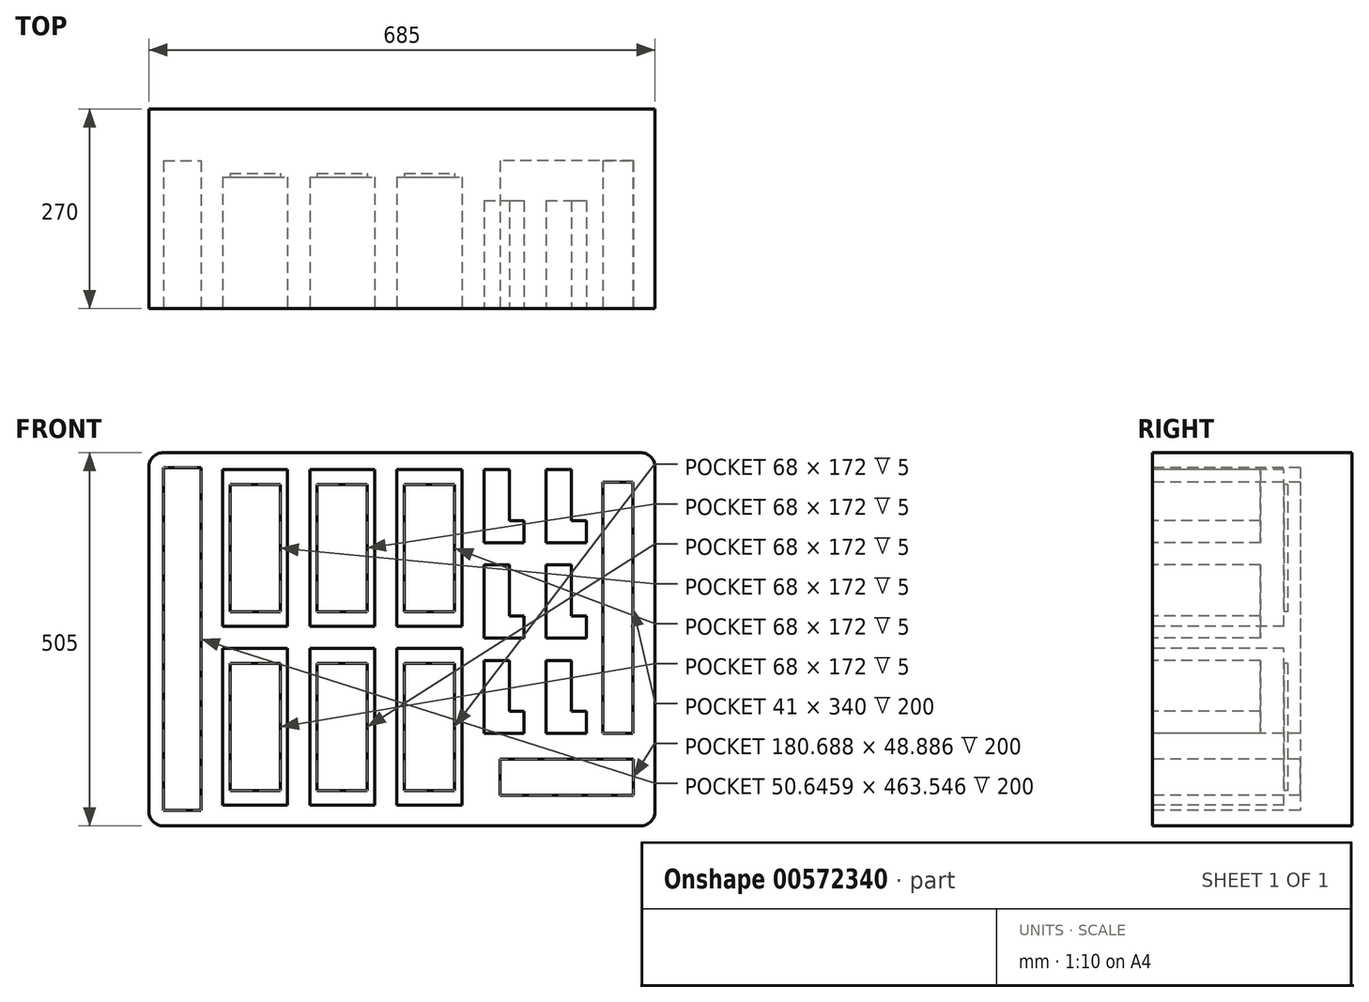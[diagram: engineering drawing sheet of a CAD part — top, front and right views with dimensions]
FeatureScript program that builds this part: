
annotation { "Feature Type Name" : "Feature", "Feature Type Description" : "" }
export const myFeature = defineFeature(function(context is Context, id is Id, definition is map)
    precondition{}
    {
        {
            var Q0;
            Q0=qCreatedBy(makeId("Front.planeOp"),FACE);
            var sketch = newSketch(context, id + "F0", { "sketchPlane" : qUnion([Q0])});
            skLineSegment(sketch, "E0.bottom", {"start": v(-665, 505) * mm, "end": v(-20, 505) * mm});
            skLineSegment(sketch, "E0.top", {"start": v(-665, 0) * mm, "end": v(-20, 0) * mm});
            skLineSegment(sketch, "E0.left", {"start": v(-685, 485) * mm, "end": v(-685, 20) * mm});
            skLineSegment(sketch, "E0.right", {"start": v(0, 485) * mm, "end": v(0, 20) * mm});
            skPoint(sketch, "E1.visualSharp", {"position": v(-685, 505) * mm});
            skArc(sketch, "E1.filletArc", {"start": v(-665, 505) * mm, "mid": v(-679.14, 499.14) * mm, "end": v(-685, 485) * mm});
            skPoint(sketch, "E2.visualSharp", {"position": v(-685, 0) * mm});
            skArc(sketch, "E2.filletArc", {"start": v(-685, 20) * mm, "mid": v(-679.14, 5.86) * mm, "end": v(-665, 0) * mm});
            skPoint(sketch, "E3.visualSharp", {"position": v(0, 0) * mm});
            skArc(sketch, "E3.filletArc", {"start": v(-20, 0) * mm, "mid": v(-5.86, 5.86) * mm, "end": v(0, 20) * mm});
            skPoint(sketch, "E4.visualSharp", {"position": v(0, 505) * mm});
            skArc(sketch, "E4.filletArc", {"start": v(0, 485) * mm, "mid": v(-5.86, 499.14) * mm, "end": v(-20, 505) * mm});
            skSolve(sketch);
        }
        {
            var Q0;
            Q0=makeQuery(id+"F0.imprint","IMPRINT",FACE,{"disambiguationData":[TD([[makeQuery(id+"F0.imprint","IMPRINT",EDGE,{"derivedFrom":sQuery(id+"F0.wireOp",EDGE,"E0.bottom")}),-1.0]])]});
            extrude(context, id + "F1", {"entities" : qUnion([Q0]), "oppositeDirection" : true, "depth" : 270 * mm, "offsetDistance" : 25 * mm});
        }
        {
            var Q0;
            Q0=makeQuery(id+"F1.opExtrude","CAP_FACE",FACE,{"disambiguationData":[OSD([sQuery(id+"F0.wireOp",EDGE,"E0.bottom"),sQuery(id+"F0.wireOp",EDGE,"E0.top"),sQuery(id+"F0.wireOp",EDGE,"E0.left"),sQuery(id+"F0.wireOp",EDGE,"E0.right")])],"isStart":true});
            var sketch = newSketch(context, id + "F2", { "sketchPlane" : qUnion([Q0])});
            skLineSegment(sketch, "E5.bottom", {"start": v(-585.25, 28) * mm, "end": v(-497.25, 28) * mm});
            skLineSegment(sketch, "E5.top", {"start": v(-585.25, 240) * mm, "end": v(-497.25, 240) * mm});
            skLineSegment(sketch, "E5.left", {"start": v(-585.25, 28) * mm, "end": v(-585.25, 240) * mm});
            skLineSegment(sketch, "E5.right", {"start": v(-497.25, 28) * mm, "end": v(-497.25, 240) * mm});
            skLineSegment(sketch, "E6.0.1.0", {"start": v(-497.25, 270) * mm, "end": v(-497.25, 482) * mm});
            skLineSegment(sketch, "E6.0.1.1", {"start": v(-585.25, 270) * mm, "end": v(-585.25, 482) * mm});
            skLineSegment(sketch, "E6.0.1.2", {"start": v(-585.25, 482) * mm, "end": v(-497.25, 482) * mm});
            skLineSegment(sketch, "E6.0.1.3", {"start": v(-585.25, 270) * mm, "end": v(-497.25, 270) * mm});
            skLineSegment(sketch, "E6.1.0.0", {"start": v(-379.25, 28) * mm, "end": v(-379.25, 240) * mm});
            skLineSegment(sketch, "E6.1.0.1", {"start": v(-467.25, 28) * mm, "end": v(-467.25, 240) * mm});
            skLineSegment(sketch, "E6.1.0.2", {"start": v(-467.25, 240) * mm, "end": v(-379.25, 240) * mm});
            skLineSegment(sketch, "E6.1.0.3", {"start": v(-467.25, 28) * mm, "end": v(-379.25, 28) * mm});
            skLineSegment(sketch, "E6.1.1.0", {"start": v(-379.25, 270) * mm, "end": v(-379.25, 482) * mm});
            skLineSegment(sketch, "E6.1.1.1", {"start": v(-467.25, 270) * mm, "end": v(-467.25, 482) * mm});
            skLineSegment(sketch, "E6.1.1.2", {"start": v(-467.25, 482) * mm, "end": v(-379.25, 482) * mm});
            skLineSegment(sketch, "E6.1.1.3", {"start": v(-467.25, 270) * mm, "end": v(-379.25, 270) * mm});
            skLineSegment(sketch, "E6.2.0.0", {"start": v(-261.25, 28) * mm, "end": v(-261.25, 240) * mm});
            skLineSegment(sketch, "E6.2.0.1", {"start": v(-349.25, 28) * mm, "end": v(-349.25, 240) * mm});
            skLineSegment(sketch, "E6.2.0.2", {"start": v(-349.25, 240) * mm, "end": v(-261.25, 240) * mm});
            skLineSegment(sketch, "E6.2.0.3", {"start": v(-349.25, 28) * mm, "end": v(-261.25, 28) * mm});
            skLineSegment(sketch, "E6.2.1.0", {"start": v(-261.25, 270) * mm, "end": v(-261.25, 482) * mm});
            skLineSegment(sketch, "E6.2.1.1", {"start": v(-349.25, 270) * mm, "end": v(-349.25, 482) * mm});
            skLineSegment(sketch, "E6.2.1.2", {"start": v(-349.25, 482) * mm, "end": v(-261.25, 482) * mm});
            skLineSegment(sketch, "E6.2.1.3", {"start": v(-349.25, 270) * mm, "end": v(-261.25, 270) * mm});
            skLineSegment(sketch, "E6.direction1", {"start": v(-585.25, 28) * mm, "end": v(-467.25, 28) * mm, "construction": true});
            skLineSegment(sketch, "E6.direction2", {"start": v(-585.25, 28) * mm, "end": v(-585.25, 270) * mm, "construction": true});
            skSolve(sketch);
        }
        {
            var Q0;
            Q0=qSketchRegion(id+"F2",true);
            extrude(context, id + "F3", {"entities" : qUnion([Q0]), "operationType" : NewBodyOperationType.REMOVE, "oppositeDirection" : true, "depth" : 178 * mm, "offsetDistance" : 25 * mm});
        }
        {
            var Q0;
            Q0=makeQuery(id+"F3.boolean.opBoolean","COPY",FACE,{"derivedFrom":makeQuery(id+"F3.opExtrude","CAP_FACE",FACE,{"disambiguationData":[OSD([sQuery(id+"F2.wireOp",EDGE,"E6.0.1.0"),sQuery(id+"F2.wireOp",EDGE,"E6.0.1.1"),sQuery(id+"F2.wireOp",EDGE,"E6.0.1.2"),sQuery(id+"F2.wireOp",EDGE,"E6.0.1.3")])],"isStart":false})});
            var sketch = newSketch(context, id + "F4", { "sketchPlane" : qUnion([Q0])});
            skLineSegment(sketch, "E7.bottom", {"start": v(-575.25, 220) * mm, "end": v(-507.25, 220) * mm});
            skLineSegment(sketch, "E7.top", {"start": v(-575.25, 48) * mm, "end": v(-507.25, 48) * mm});
            skLineSegment(sketch, "E7.left", {"start": v(-575.25, 220) * mm, "end": v(-575.25, 48) * mm});
            skLineSegment(sketch, "E7.right", {"start": v(-507.25, 220) * mm, "end": v(-507.25, 48) * mm});
            skLineSegment(sketch, "E8.0.1.0", {"start": v(-507.25, 462) * mm, "end": v(-507.25, 290) * mm});
            skLineSegment(sketch, "E8.0.1.1", {"start": v(-575.25, 462) * mm, "end": v(-575.25, 290) * mm});
            skLineSegment(sketch, "E8.0.1.2", {"start": v(-575.25, 290) * mm, "end": v(-507.25, 290) * mm});
            skLineSegment(sketch, "E8.0.1.3", {"start": v(-575.25, 462) * mm, "end": v(-507.25, 462) * mm});
            skLineSegment(sketch, "E8.1.0.0", {"start": v(-389.25, 220) * mm, "end": v(-389.25, 48) * mm});
            skLineSegment(sketch, "E8.1.0.1", {"start": v(-457.25, 220) * mm, "end": v(-457.25, 48) * mm});
            skLineSegment(sketch, "E8.1.0.2", {"start": v(-457.25, 48) * mm, "end": v(-389.25, 48) * mm});
            skLineSegment(sketch, "E8.1.0.3", {"start": v(-457.25, 220) * mm, "end": v(-389.25, 220) * mm});
            skLineSegment(sketch, "E8.1.1.0", {"start": v(-389.25, 462) * mm, "end": v(-389.25, 290) * mm});
            skLineSegment(sketch, "E8.1.1.1", {"start": v(-457.25, 462) * mm, "end": v(-457.25, 290) * mm});
            skLineSegment(sketch, "E8.1.1.2", {"start": v(-457.25, 290) * mm, "end": v(-389.25, 290) * mm});
            skLineSegment(sketch, "E8.1.1.3", {"start": v(-457.25, 462) * mm, "end": v(-389.25, 462) * mm});
            skLineSegment(sketch, "E8.2.0.0", {"start": v(-271.25, 220) * mm, "end": v(-271.25, 48) * mm});
            skLineSegment(sketch, "E8.2.0.1", {"start": v(-339.25, 220) * mm, "end": v(-339.25, 48) * mm});
            skLineSegment(sketch, "E8.2.0.2", {"start": v(-339.25, 48) * mm, "end": v(-271.25, 48) * mm});
            skLineSegment(sketch, "E8.2.0.3", {"start": v(-339.25, 220) * mm, "end": v(-271.25, 220) * mm});
            skLineSegment(sketch, "E8.2.1.0", {"start": v(-271.25, 462) * mm, "end": v(-271.25, 290) * mm});
            skLineSegment(sketch, "E8.2.1.1", {"start": v(-339.25, 462) * mm, "end": v(-339.25, 290) * mm});
            skLineSegment(sketch, "E8.2.1.2", {"start": v(-339.25, 290) * mm, "end": v(-271.25, 290) * mm});
            skLineSegment(sketch, "E8.2.1.3", {"start": v(-339.25, 462) * mm, "end": v(-271.25, 462) * mm});
            skLineSegment(sketch, "E8.direction1", {"start": v(-575.25, 48) * mm, "end": v(-457.25, 48) * mm, "construction": true});
            skLineSegment(sketch, "E8.direction2", {"start": v(-575.25, 48) * mm, "end": v(-575.25, 290) * mm, "construction": true});
            skSolve(sketch);
        }
        {
            var Q0;
            Q0=makeQuery(id+"F4.imprint","IMPRINT",FACE,{"disambiguationData":[TD([[makeQuery(id+"F4.imprint","IMPRINT",EDGE,{"derivedFrom":sQuery(id+"F4.wireOp",EDGE,"E8.0.1.0")}),-1.0]])]});
            var Q1;
            Q1=makeQuery(id+"F4.imprint","IMPRINT",FACE,{"disambiguationData":[TD([[makeQuery(id+"F4.imprint","IMPRINT",EDGE,{"derivedFrom":sQuery(id+"F4.wireOp",EDGE,"E8.1.1.0")}),-1.0]])]});
            var Q2;
            Q2=makeQuery(id+"F4.imprint","IMPRINT",FACE,{"disambiguationData":[TD([[makeQuery(id+"F4.imprint","IMPRINT",EDGE,{"derivedFrom":sQuery(id+"F4.wireOp",EDGE,"E8.2.1.0")}),-1.0]])]});
            var Q3;
            Q3=makeQuery(id+"F4.imprint","IMPRINT",FACE,{"disambiguationData":[TD([[makeQuery(id+"F4.imprint","IMPRINT",EDGE,{"derivedFrom":sQuery(id+"F4.wireOp",EDGE,"E8.2.0.0")}),-1.0]])]});
            var Q4;
            Q4=makeQuery(id+"F4.imprint","IMPRINT",FACE,{"disambiguationData":[TD([[makeQuery(id+"F4.imprint","IMPRINT",EDGE,{"derivedFrom":sQuery(id+"F4.wireOp",EDGE,"E8.1.0.0")}),-1.0]])]});
            var Q5;
            Q5=makeQuery(id+"F4.imprint","IMPRINT",FACE,{"disambiguationData":[TD([[makeQuery(id+"F4.imprint","IMPRINT",EDGE,{"derivedFrom":sQuery(id+"F4.wireOp",EDGE,"E7.bottom")}),-1.0]])]});
            extrude(context, id + "F5", {"entities" : qUnion([Q0, Q1, Q2, Q3, Q4, Q5]), "operationType" : NewBodyOperationType.REMOVE, "oppositeDirection" : true, "depth" : 5 * mm, "offsetDistance" : 25 * mm});
        }
        {
            var Q0;
            Q0=makeQuery(id+"F1.opExtrude","CAP_FACE",FACE,{"disambiguationData":[OSD([sQuery(id+"F0.wireOp",EDGE,"E0.bottom"),sQuery(id+"F0.wireOp",EDGE,"E0.top"),sQuery(id+"F0.wireOp",EDGE,"E0.left"),sQuery(id+"F0.wireOp",EDGE,"E0.right"),sQuery(id+"F0.wireOp",EDGE,"E1.filletArc"),sQuery(id+"F0.wireOp",EDGE,"E2.filletArc"),sQuery(id+"F0.wireOp",EDGE,"E3.filletArc"),sQuery(id+"F0.wireOp",EDGE,"E4.filletArc")])],"isStart":true});
            var sketch = newSketch(context, id + "F6", { "sketchPlane" : qUnion([Q0])});
            skLineSegment(sketch, "E9", {"start": v(-231.25, 383) * mm, "end": v(-231.25, 482) * mm});
            skLineSegment(sketch, "E10", {"start": v(-231.25, 482) * mm, "end": v(-197.25, 482) * mm});
            skLineSegment(sketch, "E11", {"start": v(-197.25, 482) * mm, "end": v(-197.25, 413) * mm});
            skLineSegment(sketch, "E12", {"start": v(-197.25, 413) * mm, "end": v(-177.25, 413) * mm});
            skLineSegment(sketch, "E13", {"start": v(-231.25, 383) * mm, "end": v(-177.25, 383) * mm});
            skLineSegment(sketch, "E14", {"start": v(-177.25, 413) * mm, "end": v(-177.25, 383) * mm});
            skLineSegment(sketch, "E15.0.1.0", {"start": v(-231.25, 254) * mm, "end": v(-231.25, 353) * mm});
            skLineSegment(sketch, "E15.0.1.1", {"start": v(-231.25, 353) * mm, "end": v(-197.25, 353) * mm});
            skLineSegment(sketch, "E15.0.1.2", {"start": v(-197.25, 353) * mm, "end": v(-197.25, 284) * mm});
            skLineSegment(sketch, "E15.0.1.3", {"start": v(-231.25, 254) * mm, "end": v(-177.25, 254) * mm});
            skLineSegment(sketch, "E15.0.1.4", {"start": v(-177.25, 284) * mm, "end": v(-177.25, 254) * mm});
            skLineSegment(sketch, "E15.0.1.5", {"start": v(-197.25, 284) * mm, "end": v(-177.25, 284) * mm});
            skLineSegment(sketch, "E15.0.2.0", {"start": v(-231.25, 125) * mm, "end": v(-231.25, 224) * mm});
            skLineSegment(sketch, "E15.0.2.1", {"start": v(-231.25, 224) * mm, "end": v(-197.25, 224) * mm});
            skLineSegment(sketch, "E15.0.2.2", {"start": v(-197.25, 224) * mm, "end": v(-197.25, 155) * mm});
            skLineSegment(sketch, "E15.0.2.3", {"start": v(-231.25, 125) * mm, "end": v(-177.25, 125) * mm});
            skLineSegment(sketch, "E15.0.2.4", {"start": v(-177.25, 155) * mm, "end": v(-177.25, 125) * mm});
            skLineSegment(sketch, "E15.0.2.5", {"start": v(-197.25, 155) * mm, "end": v(-177.25, 155) * mm});
            skLineSegment(sketch, "E15.1.0.0", {"start": v(-147.25, 383) * mm, "end": v(-147.25, 482) * mm});
            skLineSegment(sketch, "E15.1.0.1", {"start": v(-147.25, 482) * mm, "end": v(-113.25, 482) * mm});
            skLineSegment(sketch, "E15.1.0.2", {"start": v(-113.25, 482) * mm, "end": v(-113.25, 413) * mm});
            skLineSegment(sketch, "E15.1.0.3", {"start": v(-147.25, 383) * mm, "end": v(-93.25, 383) * mm});
            skLineSegment(sketch, "E15.1.0.4", {"start": v(-93.25, 413) * mm, "end": v(-93.25, 383) * mm});
            skLineSegment(sketch, "E15.1.0.5", {"start": v(-113.25, 413) * mm, "end": v(-93.25, 413) * mm});
            skLineSegment(sketch, "E15.1.1.0", {"start": v(-147.25, 254) * mm, "end": v(-147.25, 353) * mm});
            skLineSegment(sketch, "E15.1.1.1", {"start": v(-147.25, 353) * mm, "end": v(-113.25, 353) * mm});
            skLineSegment(sketch, "E15.1.1.2", {"start": v(-113.25, 353) * mm, "end": v(-113.25, 284) * mm});
            skLineSegment(sketch, "E15.1.1.3", {"start": v(-147.25, 254) * mm, "end": v(-93.25, 254) * mm});
            skLineSegment(sketch, "E15.1.1.4", {"start": v(-93.25, 284) * mm, "end": v(-93.25, 254) * mm});
            skLineSegment(sketch, "E15.1.1.5", {"start": v(-113.25, 284) * mm, "end": v(-93.25, 284) * mm});
            skLineSegment(sketch, "E15.1.2.0", {"start": v(-147.25, 125) * mm, "end": v(-147.25, 224) * mm});
            skLineSegment(sketch, "E15.1.2.1", {"start": v(-147.25, 224) * mm, "end": v(-113.25, 224) * mm});
            skLineSegment(sketch, "E15.1.2.2", {"start": v(-113.25, 224) * mm, "end": v(-113.25, 155) * mm});
            skLineSegment(sketch, "E15.1.2.3", {"start": v(-147.25, 125) * mm, "end": v(-93.25, 125) * mm});
            skLineSegment(sketch, "E15.1.2.4", {"start": v(-93.25, 155) * mm, "end": v(-93.25, 125) * mm});
            skLineSegment(sketch, "E15.1.2.5", {"start": v(-113.25, 155) * mm, "end": v(-93.25, 155) * mm});
            skLineSegment(sketch, "E15.direction1", {"start": v(-231.25, 383) * mm, "end": v(-147.25, 383) * mm, "construction": true});
            skLineSegment(sketch, "E15.direction2", {"start": v(-231.25, 383) * mm, "end": v(-231.25, 254) * mm, "construction": true});
            skSolve(sketch);
        }
        {
            var Q0;
            Q0 = qSketchRegion(id + "F6", true);
            extrude(context, id + "F7", {"entities" : qUnion([Q0]), "operationType" : NewBodyOperationType.REMOVE, "oppositeDirection" : true, "depth" : 146 * mm, "offsetDistance" : 25 * mm});
        }
        {
            var Q0;
            Q0=makeQuery(id+"F1.opExtrude","CAP_FACE",FACE,{"disambiguationData":[OSD([sQuery(id+"F0.wireOp",EDGE,"E0.bottom"),sQuery(id+"F0.wireOp",EDGE,"E0.top"),sQuery(id+"F0.wireOp",EDGE,"E0.left"),sQuery(id+"F0.wireOp",EDGE,"E0.right"),sQuery(id+"F0.wireOp",EDGE,"E1.filletArc"),sQuery(id+"F0.wireOp",EDGE,"E2.filletArc"),sQuery(id+"F0.wireOp",EDGE,"E3.filletArc"),sQuery(id+"F0.wireOp",EDGE,"E4.filletArc")])],"isStart":true});
            var sketch = newSketch(context, id + "F8", { "sketchPlane" : qUnion([Q0])});
            skLineSegment(sketch, "E16.bottom", {"start": v(-71, 465) * mm, "end": v(-30, 465) * mm});
            skLineSegment(sketch, "E16.top", {"start": v(-71, 125) * mm, "end": v(-30, 125) * mm});
            skLineSegment(sketch, "E16.left", {"start": v(-30, 465) * mm, "end": v(-30, 125) * mm});
            skLineSegment(sketch, "E16.right", {"start": v(-71, 465) * mm, "end": v(-71, 125) * mm});
            skLineSegment(sketch, "E17.bottom", {"start": v(-29.38, 41.4) * mm, "end": v(-210.07, 41.4) * mm});
            skLineSegment(sketch, "E17.top", {"start": v(-29.38, 90.29) * mm, "end": v(-210.07, 90.29) * mm});
            skLineSegment(sketch, "E17.left", {"start": v(-29.38, 41.4) * mm, "end": v(-29.38, 90.29) * mm});
            skLineSegment(sketch, "E17.right", {"start": v(-210.07, 41.4) * mm, "end": v(-210.07, 90.29) * mm});
            skLineSegment(sketch, "E18.bottom", {"start": v(-665, 485) * mm, "end": v(-614.35, 485) * mm});
            skLineSegment(sketch, "E18.top", {"start": v(-665, 21.45) * mm, "end": v(-614.35, 21.45) * mm});
            skLineSegment(sketch, "E18.left", {"start": v(-665, 485) * mm, "end": v(-665, 21.45) * mm});
            skLineSegment(sketch, "E18.right", {"start": v(-614.35, 485) * mm, "end": v(-614.35, 21.45) * mm});
            skSolve(sketch);
        }
        {
            var Q0;
            Q0 = qSketchRegion(id + "F8", true);
            extrude(context, id + "F9", {"entities" : qUnion([Q0]), "operationType" : NewBodyOperationType.REMOVE, "oppositeDirection" : true, "depth" : 200 * mm, "offsetDistance" : 25 * mm});
        }
    });
